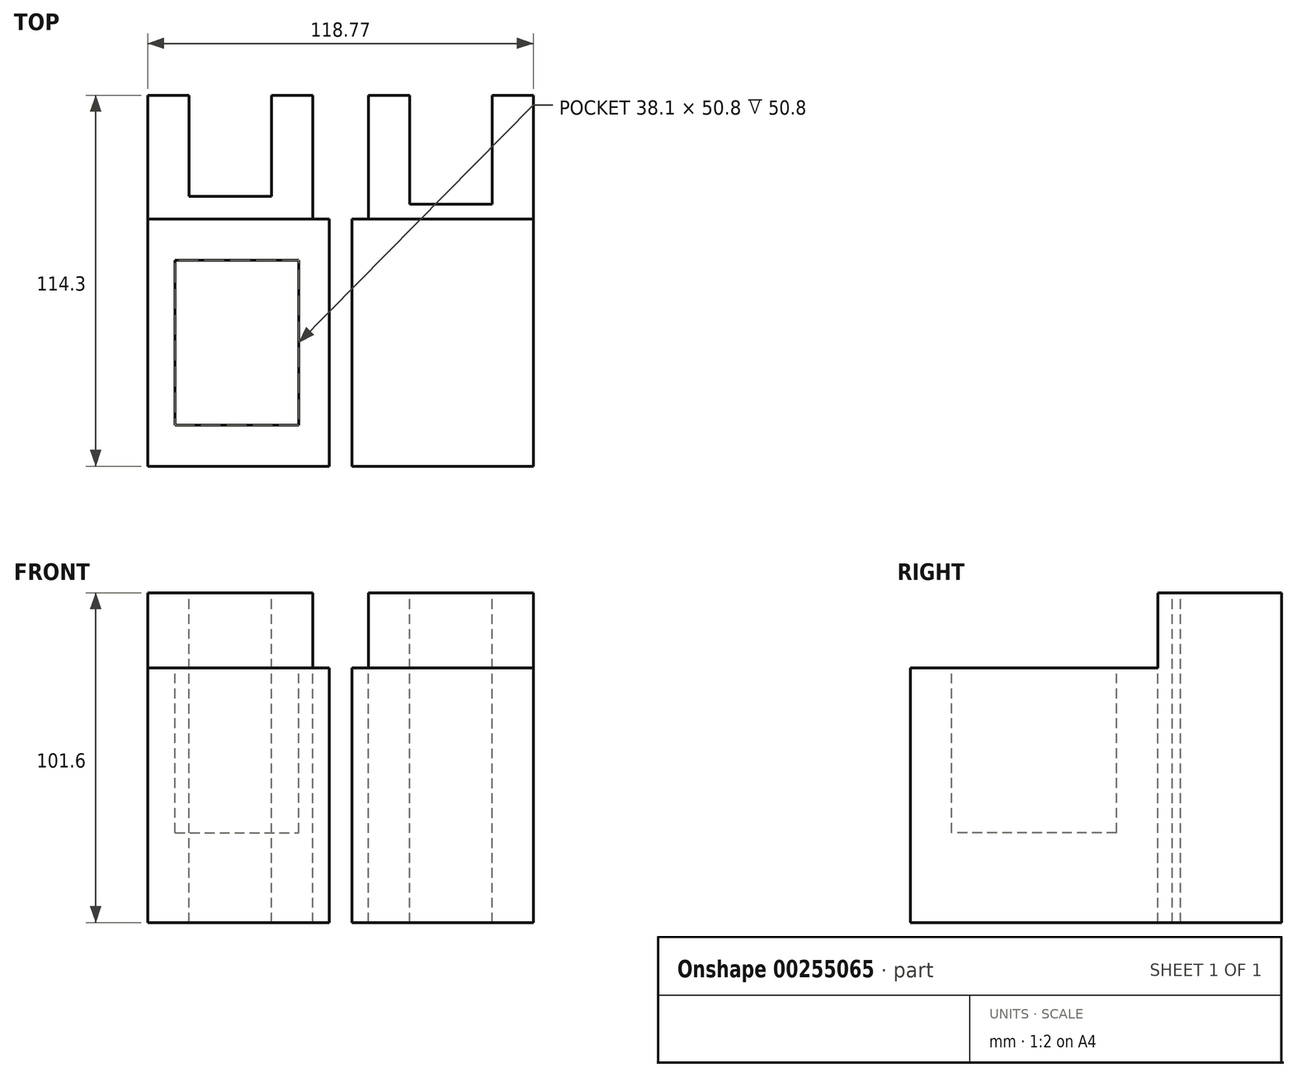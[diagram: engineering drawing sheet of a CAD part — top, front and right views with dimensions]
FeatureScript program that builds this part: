
annotation { "Feature Type Name" : "Feature", "Feature Type Description" : "" }
export const myFeature = defineFeature(function(context is Context, id is Id, definition is map)
    precondition{}
    {
        {
            var Q0;
            Q0=qCreatedBy(makeId("Top.planeOp"),FACE);
            var sketch = newSketch(context, id + "F0", { "sketchPlane" : qUnion([Q0])});
            skLineSegment(sketch, "E0.bottom", {"start": v(0, 0) * mm, "end": v(118.77, 0) * mm});
            skLineSegment(sketch, "E0.top", {"start": v(0, 56.91) * mm, "end": v(118.77, 56.91) * mm});
            skLineSegment(sketch, "E0.left", {"start": v(0, 0) * mm, "end": v(0, 56.91) * mm});
            skLineSegment(sketch, "E0.right", {"start": v(118.77, 0) * mm, "end": v(118.77, 56.91) * mm});
            skLineSegment(sketch, "E1.bottom", {"start": v(0, 0) * mm, "end": v(50.8, 0) * mm});
            skLineSegment(sketch, "E1.top", {"start": v(0, 38.1) * mm, "end": v(50.8, 38.1) * mm});
            skLineSegment(sketch, "E1.left", {"start": v(0, 0) * mm, "end": v(0, 38.1) * mm});
            skLineSegment(sketch, "E1.right", {"start": v(50.8, 0) * mm, "end": v(50.8, 38.1) * mm});
            skLineSegment(sketch, "E2.bottom", {"start": v(118.77, 0) * mm, "end": v(67.97, 0) * mm});
            skLineSegment(sketch, "E2.top", {"start": v(118.77, 38.1) * mm, "end": v(67.97, 38.1) * mm});
            skLineSegment(sketch, "E2.left", {"start": v(118.77, 0) * mm, "end": v(118.77, 38.1) * mm});
            skLineSegment(sketch, "E2.right", {"start": v(67.97, 0) * mm, "end": v(67.97, 38.1) * mm});
            skLineSegment(sketch, "E3.bottom", {"start": v(12.7, 38.1) * mm, "end": v(38.1, 38.1) * mm});
            skLineSegment(sketch, "E3.top", {"start": v(12.7, 6.97) * mm, "end": v(38.1, 6.97) * mm});
            skLineSegment(sketch, "E3.left", {"start": v(12.7, 38.1) * mm, "end": v(12.7, 6.97) * mm});
            skLineSegment(sketch, "E3.right", {"start": v(38.1, 38.1) * mm, "end": v(38.1, 6.97) * mm});
            skLineSegment(sketch, "E4.bottom", {"start": v(80.67, 38.1) * mm, "end": v(106.07, 38.1) * mm});
            skLineSegment(sketch, "E4.top", {"start": v(80.67, 4.45) * mm, "end": v(106.07, 4.45) * mm});
            skLineSegment(sketch, "E4.left", {"start": v(80.67, 38.1) * mm, "end": v(80.67, 4.45) * mm});
            skLineSegment(sketch, "E4.right", {"start": v(106.07, 38.1) * mm, "end": v(106.07, 4.45) * mm});
            skSolve(sketch);
        }
        {
            var Q0;
            Q0=makeQuery(id+"F0.imprint","IMPRINT",FACE,{"disambiguationData":[TD([[makeQuery(id+"F0.imprint","IMPRINT",EDGE,{"derivedFrom":sQuery(id+"F0.wireOp",EDGE,"E0.bottom")}),1.0]])]});
            var Q1;
            Q1=makeQuery(id+"F0.imprint","IMPRINT",FACE,{"disambiguationData":[TD([[makeQuery(id+"F0.imprint","IMPRINT",EDGE,{"derivedFrom":sQuery(id+"F0.wireOp",EDGE,"E2.bottom")}),-1.0]])]});
            var Q2;
            Q2=makeQuery(id+"F0.imprint","IMPRINT",FACE,{"disambiguationData":[TD([[makeQuery(id+"F0.imprint","IMPRINT",EDGE,{"derivedFrom":sQuery(id+"F0.wireOp",EDGE,"E1.bottom")}),1.0]])]});
            var Q3;
            Q3=makeQuery(id+"F0.imprint","IMPRINT",FACE,{"disambiguationData":[TD([[makeQuery(id+"F0.imprint","IMPRINT",EDGE,{"derivedFrom":sQuery(id+"F0.wireOp",EDGE,"E3.bottom")}),-1.0]])]});
            var Q4;
            Q4=makeQuery(id+"F0.imprint","IMPRINT",FACE,{"disambiguationData":[TD([[makeQuery(id+"F0.imprint","IMPRINT",EDGE,{"derivedFrom":sQuery(id+"F0.wireOp",EDGE,"E4.bottom")}),-1.0]])]});
            extrude(context, id + "F1", {"entities" : qUnion([Q0, Q1, Q2, Q3, Q4]), "oppositeDirection" : true, "depth" : 101.6 * mm});
        }
        {
            var Q0;
            Q0=makeQuery(id+"F1.opExtrude","SWEPT_FACE",FACE,{"disambiguationData":[OSD([sQuery(id+"F0.wireOp",EDGE,"E0.bottom"),sQuery(id+"F0.wireOp",EDGE,"E1.bottom"),sQuery(id+"F0.wireOp",EDGE,"E2.bottom")])]});
            var sketch = newSketch(context, id + "F2", { "sketchPlane" : qUnion([Q0])});
            skLineSegment(sketch, "E5.bottom", {"start": v(0, -101.6) * mm, "end": v(55.88, -101.6) * mm});
            skLineSegment(sketch, "E5.top", {"start": v(0, -23.12) * mm, "end": v(55.88, -23.12) * mm});
            skLineSegment(sketch, "E5.left", {"start": v(0, -101.6) * mm, "end": v(0, -23.12) * mm});
            skLineSegment(sketch, "E5.right", {"start": v(55.88, -101.6) * mm, "end": v(55.88, -23.12) * mm});
            skLineSegment(sketch, "E6.bottom", {"start": v(118.77, -101.6) * mm, "end": v(62.89, -101.6) * mm});
            skLineSegment(sketch, "E6.top", {"start": v(118.77, -23.12) * mm, "end": v(62.89, -23.12) * mm});
            skLineSegment(sketch, "E6.left", {"start": v(118.77, -101.6) * mm, "end": v(118.77, -23.12) * mm});
            skLineSegment(sketch, "E6.right", {"start": v(62.89, -101.6) * mm, "end": v(62.89, -23.12) * mm});
            skSolve(sketch);
        }
        {
            var Q0;
            Q0 = qSketchRegion(id + "F2", true);
            extrude(context, id + "F3", {"entities" : qUnion([Q0]), "operationType" : NewBodyOperationType.ADD, "depth" : 76.2 * mm});
        }
        {
            var Q0;
            Q0=makeQuery(id+"F3.opExtrude","SWEPT_FACE",FACE,{"disambiguationData":[OSD([sQuery(id+"F2.wireOp",EDGE,"E5.top")])]});
            var sketch = newSketch(context, id + "F4", { "sketchPlane" : qUnion([Q0])});
            skLineSegment(sketch, "E7.bottom", {"start": v(8.42, -12.7) * mm, "end": v(46.52, -12.7) * mm});
            skLineSegment(sketch, "E7.top", {"start": v(8.42, -63.5) * mm, "end": v(46.52, -63.5) * mm});
            skLineSegment(sketch, "E7.left", {"start": v(8.42, -12.7) * mm, "end": v(8.42, -63.5) * mm});
            skLineSegment(sketch, "E7.right", {"start": v(46.52, -12.7) * mm, "end": v(46.52, -63.5) * mm});
            skLineSegment(sketch, "E8", {"start": v(0, -38.1) * mm, "end": v(55.88, -38.1) * mm});
            skSolve(sketch);
        }
        {
            var Q0;
            {var subQ0=sQuery(id+"F4.wireOp",EDGE,"E7.bottom");Q0=makeQuery(id+"F4.imprint","IMPRINT",FACE,{"disambiguationData":[TD([[makeQuery(id+"F4.imprint","IMPRINT",EDGE,{"derivedFrom":subQ0}),-1.0]])]});}
            var Q1;
            {var subQ0=sQuery(id+"F4.wireOp",EDGE,"E7.top");Q1=makeQuery(id+"F4.imprint","IMPRINT",FACE,{"disambiguationData":[TD([[makeQuery(id+"F4.imprint","IMPRINT",EDGE,{"derivedFrom":subQ0}),1.0]])]});}
            extrude(context, id + "F5", {"entities" : qUnion([Q0, Q1]), "operationType" : NewBodyOperationType.REMOVE, "oppositeDirection" : true, "depth" : 50.8 * mm});
        }
    });
